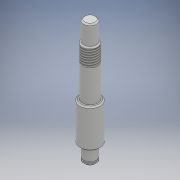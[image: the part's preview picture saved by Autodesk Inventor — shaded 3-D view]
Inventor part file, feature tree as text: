
AUTODESK INVENTOR PART (.ipt)
format: ipt  version: 2018 (Build 220112000, 112)  size: 137,728 bytes
history: native  units: mm
features: extrude x6, sketch x6, other x1, thread x1, chamfer x1
ambient origin geometry x8: Origin, YZ Plane, XZ Plane, XY Plane, X Axis, Y Axis, Z Axis, Center Point
bodies: Body1 (feature_tree)
feature tree (15):
  other  "Sólido1"
  extrude  "Extrusão1"  Depth=30.0mm TaperAngle=0.0deg
  extrude  "Extrusão2"  Depth=39.0mm TaperAngle=0.0deg
  extrude  "Extrusão3"  Depth=10.0mm TaperAngle=0.0deg
  extrude  "Extrusão4"  Depth=9.15mm TaperAngle=0.0deg
  extrude  "Extrusão5"  Depth=1.15mm TaperAngle=0.0deg
  extrude  "Extrusão6"  Depth=1.85mm TaperAngle=0.0deg
  thread  "Rosca1"  [1 undecoded]
  chamfer  "Chanfro1"  Distance=1.0mm Angle=45.0deg
  sketch  "Esboço1"  dims[d0=16.0mm d1=30.0mm d2=0.0mm]
  sketch  "Esboço2"  dims[d3=12.0mm d4=39.0mm d5=0.0mm]
  sketch  "Esboço3"  dims[d6=10.0mm d7=15.0mm d8=0.0mm]
  sketch  "Esboço4"  dims[d9=10.0mm d10=9.15mm d11=0.0mm]
  sketch  "Esboço5"  dims[d12=9.0mm d13=1.15mm d14=0.0mm]
  sketch  "Esboço6"  dims[d15=10.0mm d16=1.85mm d17=0.0mm d18=14.0mm d19=0.0mm d20=1.0mm d21=2.0mm d22=45.0deg]
note: 1 required parameter value undecoded (feature->parameter linkage not recoverable at this tier; creation-order binding heuristic only, values carry confidence <= 0.55)
